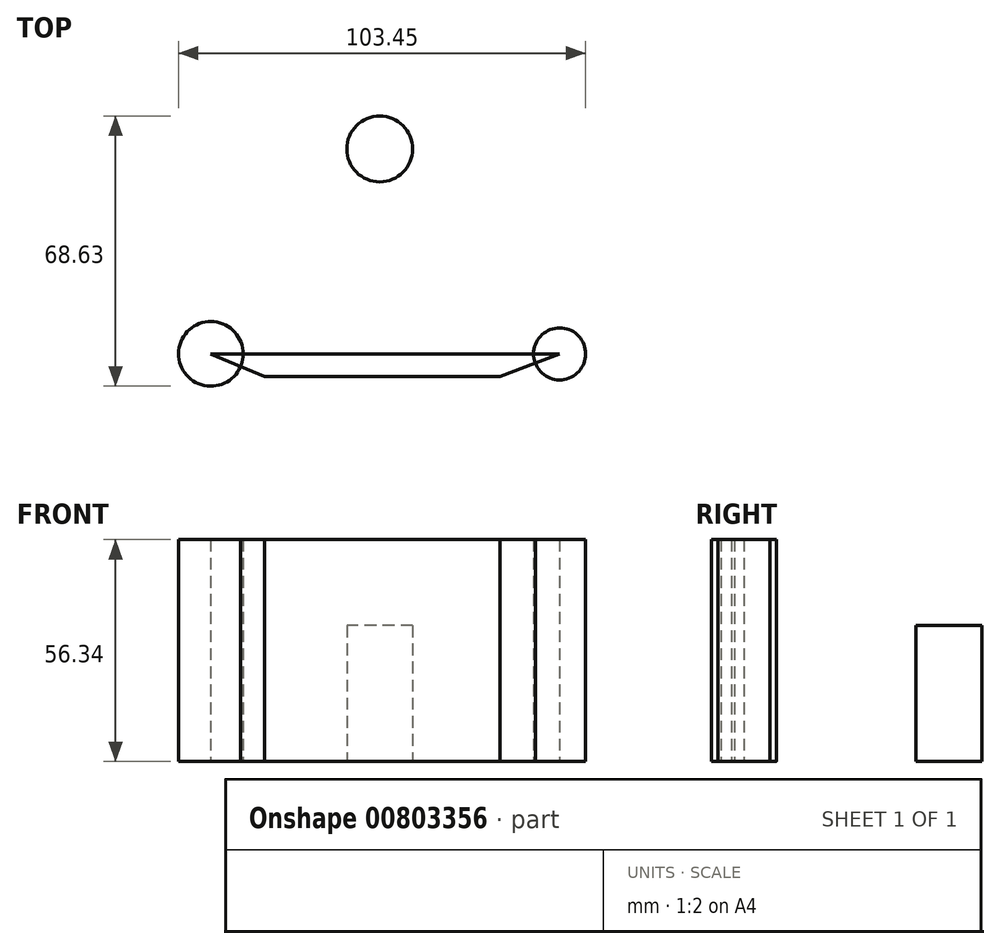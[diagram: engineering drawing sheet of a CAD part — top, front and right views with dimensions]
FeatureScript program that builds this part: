
annotation { "Feature Type Name" : "Feature", "Feature Type Description" : "" }
export const myFeature = defineFeature(function(context is Context, id is Id, definition is map)
    precondition{}
    {
        {
            var Q0;
            Q0=qCreatedBy(makeId("Top.planeOp"),FACE);
            var sketch = newSketch(context, id + "F0", { "sketchPlane" : qUnion([Q0])});
            skCircle(sketch, "E0", {"center": v(-65.65, 0) * mm, "radius": 8.2 * mm});
            skCircle(sketch, "E1", {"center": v(22.97, 0) * mm, "radius": 6.62 * mm});
            skLineSegment(sketch, "E2", {"start": v(-65.65, 0) * mm, "end": v(22.97, 0) * mm});
            skLineSegment(sketch, "E3", {"start": v(-65.65, 0) * mm, "end": v(-52, -5.8) * mm});
            skLineSegment(sketch, "E4", {"start": v(-52, -5.8) * mm, "end": v(7.84, -5.8) * mm});
            skLineSegment(sketch, "E5", {"start": v(7.84, -5.8) * mm, "end": v(22.97, 0) * mm});
            skSolve(sketch);
        }
        {
            var Q0;
            {var subQ0=sQuery(id+"F0.wireOp",EDGE,"E2");var subQ1=sQuery(id+"F0.wireOp",EDGE,"E0");var subQ2=makeQuery(id+"F0.imprint","INTERSECT",VERTEX,{"derivedFrom":[subQ1,subQ0]});Q0=makeQuery(id+"F0.imprint","IMPRINT",FACE,{"disambiguationData":[TD([[makeQuery(id+"F0.imprint","IMPRINT",EDGE,{"disambiguationData":[TD([[subQ2,-1.0]])],"derivedFrom":subQ1}),1.0]])]});}
            var Q1;
            {var subQ0=sQuery(id+"F0.wireOp",EDGE,"E4");Q1=makeQuery(id+"F0.imprint","IMPRINT",FACE,{"disambiguationData":[TD([[makeQuery(id+"F0.imprint","IMPRINT",EDGE,{"derivedFrom":subQ0}),1.0]])]});}
            var Q2;
            {var subQ0=sQuery(id+"F0.wireOp",EDGE,"E2");var subQ1=sQuery(id+"F0.wireOp",EDGE,"E1");var subQ2=makeQuery(id+"F0.imprint","INTERSECT",VERTEX,{"derivedFrom":[subQ1,subQ0]});Q2=makeQuery(id+"F0.imprint","IMPRINT",FACE,{"disambiguationData":[TD([[makeQuery(id+"F0.imprint","IMPRINT",EDGE,{"disambiguationData":[TD([[subQ2,1.0]])],"derivedFrom":subQ1}),1.0]])]});}
            var Q3;
            Q3=sQuery(id+"F0.wireOp",EDGE,"E2");
            var Q4;
            Q4=sQuery(id+"F0.wireOp",EDGE,"E0");
            var Q5;
            Q5=sQuery(id+"F0.wireOp",EDGE,"E3");
            var Q6;
            Q6=sQuery(id+"F0.wireOp",EDGE,"E4");
            var Q7;
            Q7=sQuery(id+"F0.wireOp",EDGE,"E1");
            var Q8;
            Q8=sQuery(id+"F0.wireOp",EDGE,"E5");
            extrude(context, id + "F1", {"entities" : qUnion([Q0, Q1, Q2]), "surfaceEntities" : qUnion([Q3, Q4, Q5, Q6, Q7, Q8]), "depth" : 56.34 * mm, "offsetDistance" : 25.4 * mm});
        }
        {
            var Q0;
            Q0=qCreatedBy(makeId("Top.planeOp"),FACE);
            var sketch = newSketch(context, id + "F2", { "sketchPlane" : qUnion([Q0])});
            skCircle(sketch, "E6", {"center": v(-22.73, 52.06) * mm, "radius": 8.36 * mm});
            skCircle(sketch, "E7", {"center": v(13.32, 49.25) * mm, "radius": 11.1 * mm});
            skCircle(sketch, "E8", {"center": v(13.32, 49.25) * mm, "radius": 1.97 * mm});
            skSolve(sketch);
        }
        {
            var Q0;
            Q0=makeQuery(id+"F2.imprint","IMPRINT",FACE,{"disambiguationData":[TD([[makeQuery(id+"F2.imprint","IMPRINT",EDGE,{"derivedFrom":sQuery(id+"F2.wireOp",EDGE,"E6")}),1.0]])]});
            extrude(context, id + "F3", {"entities" : qUnion([Q0]), "depth" : 9.16 * mm, "offsetDistance" : 25.4 * mm});
        }
        {
            var Q0;
            Q0=makeQuery(id+"F3.opExtrude","CAP_FACE",FACE,{"disambiguationData":[OSD([sQuery(id+"F2.wireOp",EDGE,"E6")])],"isStart":false});
            extrude(context, id + "F4", {"entities" : qUnion([Q0]), "operationType" : NewBodyOperationType.ADD, "depth" : 25.4 * mm, "offsetDistance" : 25.4 * mm});
        }
    });
